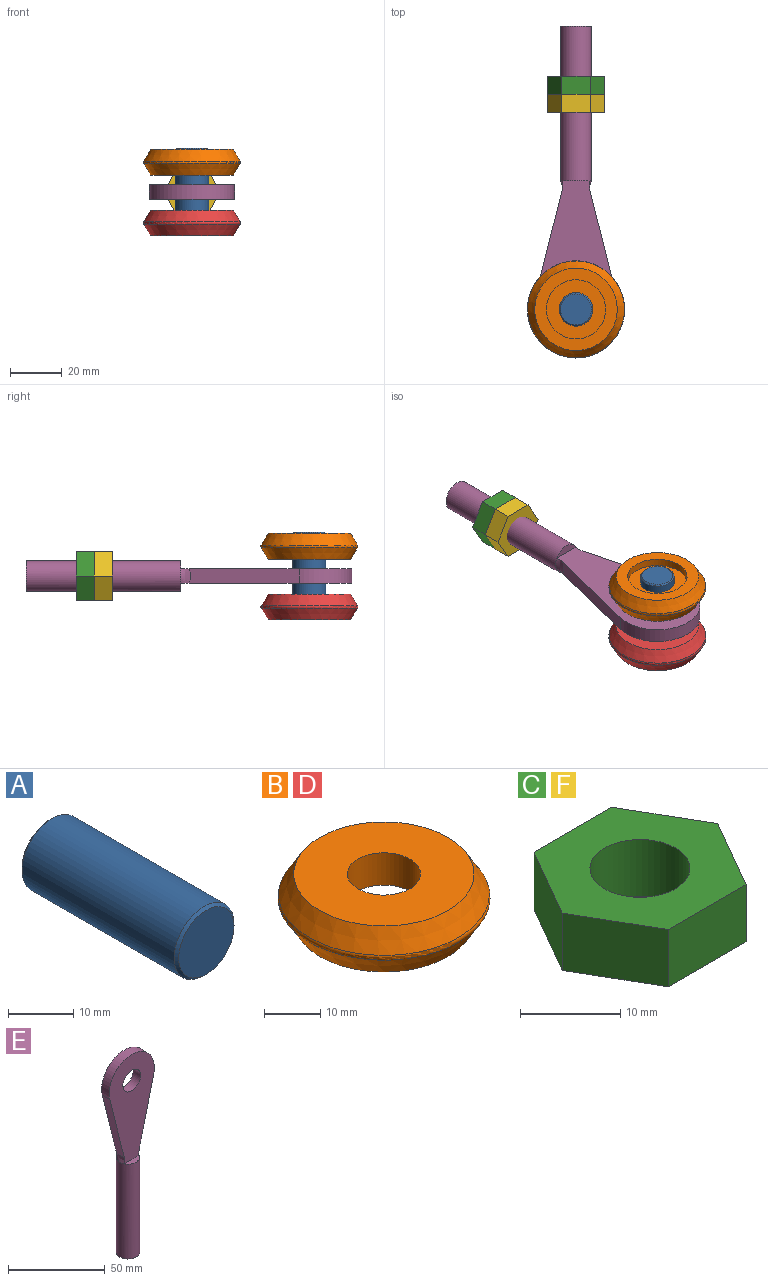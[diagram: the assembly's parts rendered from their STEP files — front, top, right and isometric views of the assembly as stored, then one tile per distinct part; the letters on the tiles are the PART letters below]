
ASSEMBLY  parts=6 mates=5
PART A: 5 faces, bbox 13x34x13 mm
  f0: cylinder r=6.5mm len=33mm, axis (0,1,0), area 1347.7mm2, adj f3,f4
  f1: plane 12x12mm, normal (0,-1,0), area 113.1mm2, adj f4
  f2: plane 12x12mm, normal (0,1,0), area 113.1mm2, adj f3
  f3: cone r=6.5mm half-angle=45deg, axis (0,-1,0), area 27.8mm2, adj f0,f2
  f4: cone r=6mm half-angle=45deg, axis (0,1,0), area 27.8mm2, adj f0,f1
PART B: 8 faces, bbox 40.8x40.8x10 mm
  f0: cylinder r=11.5mm len=23mm, axis (0,0,1), area 216.8mm2, adj f2,f7
  f1: plane 32x32mm, normal (0,0,1), area 671.5mm2, adj f4,f6
  f2: plane 32x32mm, normal (0,0,-1), area 388.8mm2, adj f0,f3
  f3: cone r=16mm half-angle=31deg, axis (0,0,1), area 570.1mm2, adj f2,f5
  f4: cone r=16mm half-angle=31deg, axis (0,0,-1), area 570.1mm2, adj f1,f5
  f5: torus R=17.83mm, axis (0,0,-1), area 127.6mm2, adj f3,f4
  f6: cylinder r=6.5mm len=13mm, axis (0,0,-1), area 285.9mm2, adj f1,f7
  f7: plane 23x23mm, normal (0,0,-1), area 282.7mm2, adj f0,f6
PART C: 9 faces, bbox 21.9x19x7 mm
  f0: plane 9.5x7mm, normal (0.87,0.5,0), area 76.8mm2, adj f1,f6,f7,f8
  f1: plane 10.97x7mm, normal (0,1,0), area 76.8mm2, adj f0,f2,f7,f8
  f2: plane 9.5x7mm, normal (-0.87,0.5,0), area 76.8mm2, adj f1,f3,f7,f8
  f3: plane 9.5x7mm, normal (-0.87,-0.5,0), area 76.8mm2, adj f2,f4,f7,f8
  f4: plane 10.97x7mm, normal (0,-1,0), area 76.8mm2, adj f3,f6,f7,f8
  f5: cylinder r=5mm len=10mm, axis (0,0,-1), area 219.9mm2, adj f7,f8
  f6: plane 9.5x7mm, normal (0.87,-0.5,0), area 76.8mm2, adj f0,f4,f7,f8
  f7: plane 21.94x19mm, normal (0,0,1), area 234.1mm2, adj f0,f1,f2,f3,f4,f5,f6
  f8: plane 21.94x19mm, normal (0,0,-1), area 234.1mm2, adj f0,f1,f2,f3,f4,f5,f6
PART D: same geometry as B
PART E: 12 faces, bbox 33.9x12.9x127.4 mm
  f0: plane 10.67x3.25mm, normal (0,0,1), area 24.7mm2, adj f1,f7
  f1: cylinder r=6mm len=60mm, axis (0,0,-1), area 2261.9mm2, adj f0,f2,f3,f9,f10
  f2: plane 10.67x3.25mm, normal (0,0,1), area 24.7mm2, adj f1,f8
  f3: plane 12x12mm, normal (0,0,-1), area 113.1mm2, adj f1
  f4: plane 42.6x10.71mm, normal (-0.97,0,-0.24), area 239.8mm2, adj f6,f7,f8,f9
  f5: plane 42.6x10.71mm, normal (0.97,0,-0.24), area 239.8mm2, adj f6,f7,f8,f10
  f6: cylinder r=16.5mm len=33mm, axis (0,1,0), area 329.8mm2, adj f4,f5,f7,f8
  f7: plane 67.42x33.92mm, normal (0,-1,0), area 1368.5mm2, adj f0,f4,f5,f6,f9,f10,f11
  f8: plane 67.41x33.91mm, normal (0,1,0), area 1368.5mm2, adj f2,f4,f5,f6,f9,f10,f11
  f9: bspline ~10.57x3.84mm, area 22.6mm2, adj f1,f4,f7,f8
  f10: bspline ~10.57x3.84mm, area 22.6mm2, adj f1,f5,f7,f8
  f11: cylinder r=6.5mm len=13mm, axis (0,-1,0), area 224.6mm2, adj f7,f8
PART F: same geometry as C
PLACE A rot(axis=(1,0,0),90deg) t=(-34.15,-18.94,13.17)mm
PLACE B rot(axis=(-0.54,-0.84,0),180deg) t=(-34.15,-18.94,24.67)mm
PLACE C rot(axis=(1,0,0),90deg) t=(-34.15,71.56,13.17)mm
PLACE D t=(-34.15,-18.94,1.17)mm
PLACE E rot(axis=(1,0,0),90deg) t=(-34.15,61.06,13.17)mm fixed
PLACE F rot(axis=(1,0,0),90deg) t=(-34.15,64.56,13.17)mm
MATE revolute A.f0 <-> B.f0  axis (0,0,1) through (-34.15,-18.94,29.67)mm
MATE fastened E.f1 <-> F.f5  axis (0,1,0) through (-34.15,61.06,13.17)mm
MATE fastened A.f0 <-> E.f6  axis (0,0,1) through (-34.15,-18.94,13.17)mm
MATE revolute A.f0 <-> D.f0  axis (0,0,-1) through (-34.15,-18.94,-3.83)mm
MATE fastened F.f5 <-> C.f5  axis (0,1,0) through (-34.15,64.56,13.17)mm
